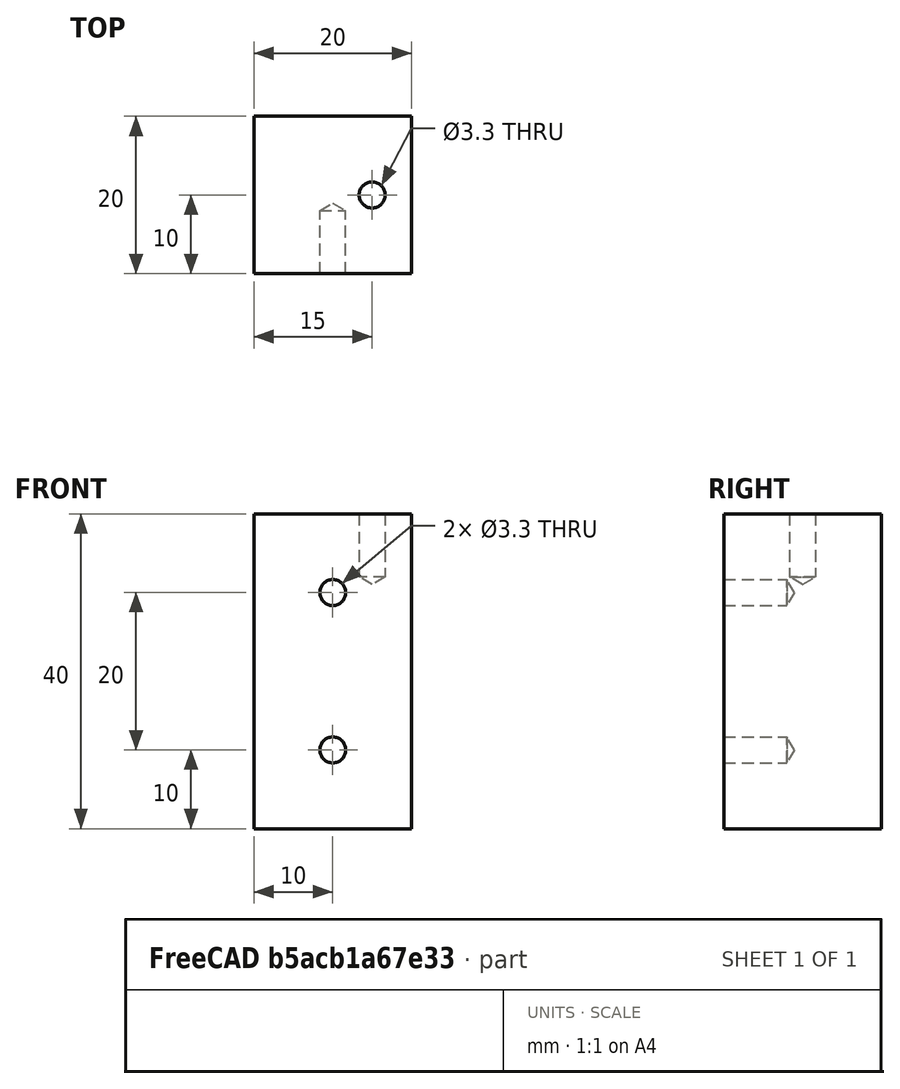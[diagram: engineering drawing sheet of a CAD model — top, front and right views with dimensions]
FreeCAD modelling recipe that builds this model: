
FCSTD DOCUMENT  (FreeCAD 1.0R39319 (Git))
Label: OCT-ULBLK-AB
License: Creative Commons Attribution 4.0
LicenseURL: https://creativecommons.org/licenses/by/4.0/
objects: TechDraw::DrawViewDimension×10, Sketcher::SketchObject×3, PartDesign::Hole×2, TechDraw::DrawProjGroupItem×2, PartDesign::Pad×1, PartDesign::Body×1, TechDraw::DrawSVGTemplate×1, TechDraw::DrawProjGroup×1, TechDraw::DrawPage×1
note: 31 computed .brp shape members not serialized (recipe doc carries the construction recipe); baked Part::Feature solids carry a one-line shape summary decoded from their .brp

FEATURE [Sketcher::SketchObject] Sketch
  ArcFitTolerance = 1e-06
  AttachmentSupport = -> [XY_Plane]
  FullyConstrained = true
  MakeInternals = false
  MapMode = 5
  sketch-geometry (4):
    g0: LineSegment StartX=-85 StartY=0 StartZ=0 EndX=-65 EndY=0 EndZ=0
    g1: LineSegment StartX=-65 StartY=0 StartZ=0 EndX=-65 EndY=20 EndZ=0
    g2: LineSegment StartX=-85 StartY=20 StartZ=0 EndX=-85 EndY=0 EndZ=0
    g3: LineSegment StartX=-65 StartY=20 StartZ=0 EndX=-85 EndY=20 EndZ=0
  constraints (12):
    c: Coincident(g0,g1)
    c: Coincident(g2,g0)
    c: Horizontal(g0)
    c: Vertical(g1)
    c: Vertical(g2)
    c: PointOnObject(g0,g-1)
    c: DistanceY(g1,g1) = 20
    c: DistanceX(g0,g0) = 20
    c: DistanceX(g0,g-1) = 85
    c: Coincident(g1,g3)
    c: Horizontal(g3)
    c: Coincident(g2,g3)
FEATURE [PartDesign::Pad] Pad
  Direction = (0,0,1)
  Length = 40
  Length2 = 10
  Profile = -> Sketch
  ReferenceAxis = -> Sketch [N_Axis]
  Suppressed = false
  Type = 0
FEATURE [Sketcher::SketchObject] Sketch001
  ArcFitTolerance = 1e-06
  AttachmentSupport = -> [Pad]
  ExternalGeometry = -> [Pad]
  FullyConstrained = true
  MakeInternals = false
  MapMode = 5
  Placement = pos=(0,0,0) rot=(1,0,0;1.5708rad)
  sketch-geometry (3):
    g0: LineSegment [constr] StartX=-75 StartY=30 StartZ=0 EndX=-75 EndY=10 EndZ=0
    g1: Circle CenterX=-75 CenterY=30 CenterZ=0 NormalX=0 NormalY=0 NormalZ=1 AngleXU=0 Radius=2
    g2: Circle CenterX=-75 CenterY=10 CenterZ=0 NormalX=0 NormalY=0 NormalZ=1 AngleXU=0 Radius=2
  constraints (8):
    c: Vertical(g0)
    c: Coincident(g1,g0)
    c: Coincident(g2,g0)
    c: Equal(g1,g2)
    c: Diameter(g1) = 4
    c: DistanceX(g0,g-1) = 75
    c: DistanceY(g-1,g0) = 10
    c: DistanceY(g0,g0) = 20
FEATURE [PartDesign::Hole] Hole
  BaseFeature = -> Pad
  CustomThreadClearance = 0
  Depth = 8
  DepthType = 0
  Diameter = 3.3
  DrillForDepth = false
  DrillPoint = 1
  DrillPointAngle = 118
  HoleCutCountersinkAngle = 90
  HoleCutCustomValues = false
  HoleCutDepth = 0
  HoleCutDiameter = 6.1
  HoleCutType = 0
  ModelThread = false
  Profile = -> Sketch001
  Suppressed = false
  Tapered = false
  TaperedAngle = 90
  ThreadClass = 0
  ThreadDepth = 8
  ThreadDepthType = 0
  ThreadDirection = 0
  ThreadFit = 0
  ThreadSize = 11
  ThreadType = 1
  Threaded = true
  UseCustomThreadClearance = false
FEATURE [Sketcher::SketchObject] Sketch002
  ArcFitTolerance = 1e-06
  AttachmentSupport = -> [Hole]
  FullyConstrained = false
  MakeInternals = false
  MapMode = 5
  Placement = pos=(0,0,40) rot=(0,0,1;0rad)
  sketch-geometry (1):
    g0: Circle CenterX=-70 CenterY=10 CenterZ=0 NormalX=0 NormalY=0 NormalZ=1 AngleXU=0 Radius=1.81729
  constraints (2):
    c: Distance(g0,g-2) = 70
    c: Distance(g0,g-1) = 10
FEATURE [PartDesign::Hole] Hole001
  BaseFeature = -> Hole
  CustomThreadClearance = 0
  Depth = 8
  DepthType = 0
  Diameter = 3.3
  DrillForDepth = false
  DrillPoint = 1
  DrillPointAngle = 118
  HoleCutCountersinkAngle = 90
  HoleCutCustomValues = false
  HoleCutDepth = 0
  HoleCutDiameter = 6.1
  HoleCutType = 0
  ModelThread = false
  Profile = -> Sketch002
  Suppressed = false
  Tapered = false
  TaperedAngle = 90
  ThreadClass = 0
  ThreadDepth = 8
  ThreadDepthType = 0
  ThreadDirection = 0
  ThreadFit = 0
  ThreadSize = 11
  ThreadType = 1
  Threaded = true
  UseCustomThreadClearance = false
FEATURE [PartDesign::Body] Body  label="OCT-ULBLK-AB"
  AllowCompound = false
  Group = -> [Sketch,Pad,Sketch001,Hole,Sketch002,Hole001]
  Origin = -> Origin
  Tip = -> Hole001
FEATURE [TechDraw::DrawSVGTemplate] Template
  EditableTexts = approval_person=S. Aphelion; creator=Michael Stoll; date_of_issue=13/02/2026; document_status=In preparation; document_type=Component Drawing; drawing_number=DN; general_tolerances=ISO 2768-m; language_code=EN; part_material=Aluminium 6082 T6; responsible_department=RD; revision_index=A; scale=2 : 1; sheet_number=1 / 1; supplementary_title_1=Upper Left Panel Block; title=OCT-ULBLK-AB
  Height = 297
  Orientation = 1
  Template = C:/Program Files/FreeCAD 1.0/data/Mod/TechDraw/Templates/A3_Landscape_ISO5457_advanced.svg
  Width = 420
FEATURE [TechDraw::DrawProjGroupItem] View  label="Front"
  CoarseView = false
  Direction = (0,-1,0)
  Focus = 100
  HardHidden = false
  IsoCount = 0
  IsoHidden = false
  IsoVisible = false
  LockPosition = true
  Perspective = false
  Rotation = 0
  RotationVector = (1,0,0)
  Scale = 2
  ScaleType = 2
  ScrubCount = 1
  SeamHidden = false
  SeamVisible = false
  SmoothHidden = false
  SmoothVisible = true
  Source = -> [Body]
  Type = 0
  X = 0
  XDirection = (1,0,0)
  Y = 0
FEATURE [TechDraw::DrawProjGroupItem] ProjItem  label="Top"
  CoarseView = false
  Direction = (0,0,1)
  Focus = 100
  HardHidden = false
  IsoCount = 0
  IsoHidden = false
  IsoVisible = false
  LockPosition = false
  Perspective = false
  Rotation = 0
  RotationVector = (1,0,0)
  Scale = 2
  ScaleType = 0
  ScrubCount = 1
  SeamHidden = false
  SeamVisible = false
  SmoothHidden = false
  SmoothVisible = true
  Source = -> [Body]
  Type = 4
  X = 0
  XDirection = (1,0,0)
  Y = 110
FEATURE [TechDraw::DrawProjGroup] ProjGroup
  Anchor = -> View
  AutoDistribute = true
  LockPosition = false
  ProjectionType = 1
  Rotation = 0
  Scale = 2
  ScaleType = 0
  Source = -> [Body]
  Views = -> [View,ProjItem]
  X = 158.571
  Y = 100.408
  spacingX = 15
  spacingY = 50
FEATURE [TechDraw::DrawViewDimension] Dimension001
  AngleOverride = false
  Arbitrary = false
  ArbitraryTolerances = false
  BoxCorners = (2) [(-20,-40,0),(20,40,0)]
  EqualTolerance = true
  ExtensionAngle = 0
  FormatSpec = %.1f
  FormatSpecOverTolerance = %+.1f
  FormatSpecUnderTolerance = %+.1f
  Inverted = false
  LineAngle = 0
  LockPosition = false
  MeasureType = 1
  OverTolerance = 0
  References2D = -> [View]
  Rotation = 0
  Scale = 2
  ScaleType = 0
  TheoreticalExact = false
  Type = 2
  UnderTolerance = 0
  X = 35.4487
  Y = 0
FEATURE [TechDraw::DrawViewDimension] Dimension003
  AngleOverride = false
  Arbitrary = false
  ArbitraryTolerances = false
  BoxCorners = (2) [(-20,-40,0),(20,40,0)]
  EqualTolerance = true
  ExtensionAngle = 0
  FormatSpec = ⌀%.1f
  FormatSpecOverTolerance = %+.1f
  FormatSpecUnderTolerance = %+.1f
  Inverted = false
  LineAngle = 0
  LockPosition = false
  MeasureType = 1
  OverTolerance = 0
  References2D = -> [View]
  Rotation = 0
  Scale = 2
  ScaleType = 0
  TheoreticalExact = false
  Type = 5
  UnderTolerance = 0
  X = -39.4185
  Y = 55.0742
FEATURE [TechDraw::DrawViewDimension] Dimension004
  AngleOverride = false
  Arbitrary = false
  ArbitraryTolerances = false
  BoxCorners = (2) [(-20,-40,0),(20,40,0)]
  EqualTolerance = true
  ExtensionAngle = 0
  FormatSpec = %.1f
  FormatSpecOverTolerance = %+.1f
  FormatSpecUnderTolerance = %+.1f
  Inverted = false
  LineAngle = 0
  LockPosition = false
  MeasureType = 1
  OverTolerance = 0
  References2D = -> [View]
  Rotation = 0
  Scale = 2
  ScaleType = 0
  TheoreticalExact = false
  Type = 0
  UnderTolerance = 0
  X = -41.2821
  Y = -30
FEATURE [TechDraw::DrawViewDimension] Dimension005
  AngleOverride = false
  Arbitrary = false
  ArbitraryTolerances = false
  BoxCorners = (2) [(-20,-40,0),(20,40,0)]
  EqualTolerance = true
  ExtensionAngle = 0
  FormatSpec = %.1f
  FormatSpecOverTolerance = %+.1f
  FormatSpecUnderTolerance = %+.1f
  Inverted = false
  LineAngle = 0
  LockPosition = false
  MeasureType = 1
  OverTolerance = 0
  References2D = -> [View]
  Rotation = 0
  Scale = 2
  ScaleType = 0
  TheoreticalExact = false
  Type = 2
  UnderTolerance = 0
  X = -41.2821
  Y = 0
FEATURE [TechDraw::DrawViewDimension] Dimension008
  AngleOverride = false
  Arbitrary = false
  ArbitraryTolerances = false
  BoxCorners = (2) [(-20,-20,0),(20,20,0)]
  EqualTolerance = true
  ExtensionAngle = 0
  FormatSpec = %.1f
  FormatSpecOverTolerance = %+.1f
  FormatSpecUnderTolerance = %+.1f
  Inverted = false
  LineAngle = 0
  LockPosition = false
  MeasureType = 1
  OverTolerance = 0
  References2D = -> [ProjItem]
  Rotation = 0
  Scale = 2
  ScaleType = 0
  TheoreticalExact = false
  Type = 2
  UnderTolerance = 0
  X = -43.6901
  Y = 0
FEATURE [TechDraw::DrawViewDimension] Dimension
  AngleOverride = false
  Arbitrary = false
  ArbitraryTolerances = false
  BoxCorners = (2) [(-20,-20,0),(20,20,0)]
  EqualTolerance = true
  ExtensionAngle = 0
  FormatSpec = ⌀%.1f
  FormatSpecOverTolerance = %+.1f
  FormatSpecUnderTolerance = %+.1f
  Inverted = false
  LineAngle = 0
  LockPosition = false
  MeasureType = 1
  OverTolerance = 0
  References2D = -> [ProjItem]
  Rotation = 0
  Scale = 2
  ScaleType = 0
  TheoreticalExact = false
  Type = 5
  UnderTolerance = 0
  X = 69.5607
  Y = 46.4278
FEATURE [TechDraw::DrawViewDimension] Dimension009
  AngleOverride = false
  Arbitrary = false
  ArbitraryTolerances = false
  BoxCorners = (2) [(-20,-20,0),(20,20,0)]
  EqualTolerance = true
  ExtensionAngle = 0
  FormatSpec = %.1f
  FormatSpecOverTolerance = %+.1f
  FormatSpecUnderTolerance = %+.1f
  Inverted = false
  LineAngle = 0
  LockPosition = false
  MeasureType = 1
  OverTolerance = 0
  References2D = -> [ProjItem]
  Rotation = 0
  Scale = 2
  ScaleType = 0
  TheoreticalExact = false
  Type = 0
  UnderTolerance = 0
  X = 43.6395
  Y = -10
FEATURE [TechDraw::DrawViewDimension] Dimension010
  AngleOverride = false
  Arbitrary = false
  ArbitraryTolerances = false
  BoxCorners = (2) [(-20,-20,0),(20,20,0)]
  EqualTolerance = true
  ExtensionAngle = 0
  FormatSpec = %.1f
  FormatSpecOverTolerance = %+.1f
  FormatSpecUnderTolerance = %+.1f
  Inverted = false
  LineAngle = 0
  LockPosition = false
  MeasureType = 1
  OverTolerance = 0
  References2D = -> [ProjItem]
  Rotation = 0
  Scale = 2
  ScaleType = 0
  TheoreticalExact = false
  Type = 0
  UnderTolerance = 0
  X = 15
  Y = 37.8942
FEATURE [TechDraw::DrawViewDimension] Dimension011
  AngleOverride = false
  Arbitrary = false
  ArbitraryTolerances = false
  BoxCorners = (2) [(-20,-40,0),(20,40,0)]
  EqualTolerance = true
  ExtensionAngle = 0
  FormatSpec = %.1f
  FormatSpecOverTolerance = %+.1f
  FormatSpecUnderTolerance = %+.1f
  Inverted = false
  LineAngle = 0
  LockPosition = false
  MeasureType = 1
  OverTolerance = 0
  References2D = -> [View]
  Rotation = 0
  Scale = 2
  ScaleType = 0
  TheoreticalExact = false
  Type = 0
  UnderTolerance = 0
  X = -10
  Y = -59.5535
FEATURE [TechDraw::DrawViewDimension] Dimension012
  AngleOverride = false
  Arbitrary = false
  ArbitraryTolerances = false
  BoxCorners = (2) [(-20,-20,0),(20,20,0)]
  EqualTolerance = true
  ExtensionAngle = 0
  FormatSpec = %.1f
  FormatSpecOverTolerance = %+.1f
  FormatSpecUnderTolerance = %+.1f
  Inverted = false
  LineAngle = 0
  LockPosition = false
  MeasureType = 1
  OverTolerance = 0
  References2D = -> [ProjItem]
  Rotation = 0
  Scale = 2
  ScaleType = 0
  TheoreticalExact = false
  Type = 1
  UnderTolerance = 0
  X = 0
  Y = -35.6881
FEATURE [TechDraw::DrawPage] Page
  KeepUpdated = true
  NextBalloonIndex = 1
  ProjectionType = 1
  Scale = 2
  Template = -> Template
  Views = -> [ProjGroup,Dimension001,Dimension003,Dimension004,Dimension005,Dimension008,Dimension,Dimension009,Dimension010,Dimension011,Dimension012]
